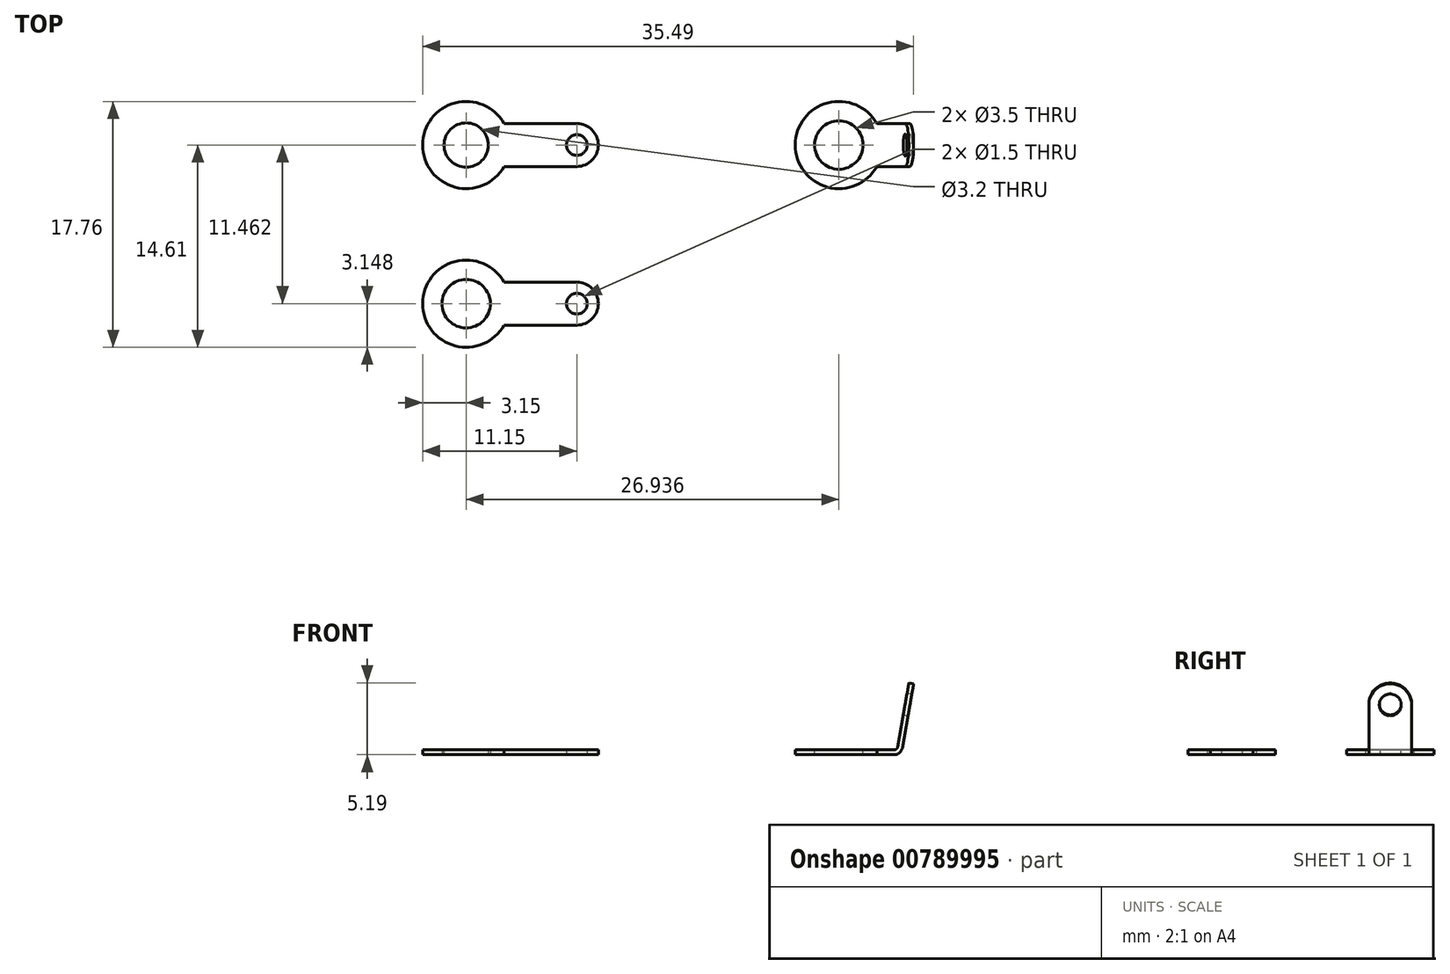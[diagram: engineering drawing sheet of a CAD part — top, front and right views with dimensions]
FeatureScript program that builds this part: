
annotation { "Feature Type Name" : "Feature", "Feature Type Description" : "" }
export const myFeature = defineFeature(function(context is Context, id is Id, definition is map)
    precondition{}
    {
        {
            var Q0;
            Q0=qCreatedBy(makeId("Top.planeOp"),FACE);
            var sketch = newSketch(context, id + "F0", { "sketchPlane" : qUnion([Q0])});
            skCircle(sketch, "E0", {"center": v(0, 0) * mm, "radius": 1.6 * mm});
            skCircle(sketch, "E1", {"center": v(0, 0) * mm, "radius": 3.15 * mm});
            skCircle(sketch, "E2", {"center": v(8, 0) * mm, "radius": 0.75 * mm});
            skCircle(sketch, "E3", {"center": v(8, 0) * mm, "radius": 1.55 * mm});
            skLineSegment(sketch, "E4", {"start": v(8, 1.55) * mm, "end": v(2.74, 1.55) * mm});
            skLineSegment(sketch, "E5", {"start": v(8, -1.55) * mm, "end": v(2.74, -1.55) * mm});
            skCircle(sketch, "E6", {"center": v(0, -11.46) * mm, "radius": 1.75 * mm});
            skCircle(sketch, "E7", {"center": v(0, -11.46) * mm, "radius": 3.15 * mm});
            skCircle(sketch, "E8", {"center": v(8, -11.46) * mm, "radius": 0.75 * mm});
            skCircle(sketch, "E9", {"center": v(8, -11.46) * mm, "radius": 1.55 * mm});
            skLineSegment(sketch, "E10", {"start": v(8, -9.91) * mm, "end": v(2.74, -9.91) * mm});
            skLineSegment(sketch, "E11", {"start": v(8, -13.01) * mm, "end": v(2.74, -13.01) * mm});
            skSolve(sketch);
        }
        {
            var Q0;
            Q0 = qSketchRegion(id + "F0", true);
            extrude(context, id + "F1", {"entities" : qUnion([Q0]), "depth" : .35 * mm, "offsetDistance" : 25 * mm});
        }
        {
            var Q0;
            Q0=qCreatedBy(makeId("Front.planeOp"),FACE);
            var sketch = newSketch(context, id + "F2", { "sketchPlane" : qUnion([Q0])});
            skLineSegment(sketch, "E12.bottom", {"start": v(23.79, 0.35) * mm, "end": v(30.94, 0.35) * mm});
            skLineSegment(sketch, "E12.top", {"start": v(23.79, 0) * mm, "end": v(30.94, 0) * mm});
            skLineSegment(sketch, "E12.left", {"start": v(23.79, 0.35) * mm, "end": v(23.79, 0) * mm});
            skLineSegment(sketch, "E12.right", {"start": v(30.94, 0.35) * mm, "end": v(30.94, 0) * mm});
            skLineSegment(sketch, "E13.bottom", {"start": v(31.18, 0.56) * mm, "end": v(31.53, 0.5) * mm});
            skLineSegment(sketch, "E13.top", {"start": v(32, 5.19) * mm, "end": v(32.34, 5.12) * mm});
            skLineSegment(sketch, "E13.left", {"start": v(31.18, 0.56) * mm, "end": v(32, 5.19) * mm});
            skLineSegment(sketch, "E13.right", {"start": v(31.53, 0.5) * mm, "end": v(32.34, 5.12) * mm});
            skLineSegment(sketch, "E14.bottom", {"start": v(25.19, 0.35) * mm, "end": v(28.69, 0.35) * mm});
            skLineSegment(sketch, "E14.top", {"start": v(25.19, 0) * mm, "end": v(28.69, 0) * mm});
            skLineSegment(sketch, "E14.left", {"start": v(25.19, 0.35) * mm, "end": v(25.19, 0) * mm});
            skLineSegment(sketch, "E14.right", {"start": v(28.69, 0.35) * mm, "end": v(28.69, 0) * mm});
            skLineSegment(sketch, "E15.bottom", {"start": v(31.87, 4.44) * mm, "end": v(32.21, 4.38) * mm});
            skLineSegment(sketch, "E15.top", {"start": v(31.6, 2.88) * mm, "end": v(31.94, 2.82) * mm});
            skLineSegment(sketch, "E15.left", {"start": v(31.87, 4.44) * mm, "end": v(31.6, 2.88) * mm});
            skLineSegment(sketch, "E15.right", {"start": v(32.21, 4.38) * mm, "end": v(31.94, 2.82) * mm});
            skCircle(sketch, "E16", {"center": v(30.94, 0.6) * mm, "radius": 0.25 * mm});
            skCircle(sketch, "E17", {"center": v(30.94, 0.6) * mm, "radius": 0.6 * mm});
            skLineSegment(sketch, "E18", {"start": v(26.94, 0.35) * mm, "end": v(26.94, 0) * mm});
            skLineSegment(sketch, "E19", {"start": v(31.73, 3.66) * mm, "end": v(32.07, 3.6) * mm});
            skLineSegment(sketch, "E20", {"start": v(26.94, 0.35) * mm, "end": v(26.94, 1.93) * mm, "construction": true});
            skLineSegment(sketch, "E21", {"start": v(31.9, 3.63) * mm, "end": v(31.73, 3.66) * mm, "construction": true});
            skPoint(sketch, "E21.endSnap0", {"position": v(31.9, 3.63) * mm});
            skSolve(sketch);
        }
        {
            var Q0;
            {var subQ0=sQuery(id+"F2.wireOp",EDGE,"E12.left");Q0=makeQuery(id+"F2.imprint","IMPRINT",FACE,{"disambiguationData":[TD([[makeQuery(id+"F2.imprint","IMPRINT",EDGE,{"derivedFrom":subQ0}),1.0]])]});}
            var Q1;
            Q1=sQuery(id+"F2.wireOp",EDGE,"E18");
            revolve(context, id + "F3", {"surfaceOperationType" : NewSurfaceOperationType.NEW, "entities" : qUnion([Q0]), "axis" : qUnion([Q1]), "revolveType" : RevolveType.FULL});
        }
        {
            var Q0;
            {var subQ0=sQuery(id+"F2.wireOp",EDGE,"E13.top");Q0=makeQuery(id+"F2.imprint","IMPRINT",FACE,{"disambiguationData":[TD([[makeQuery(id+"F2.imprint","IMPRINT",EDGE,{"derivedFrom":subQ0}),-1.0]])]});}
            var Q1;
            {var subQ0=sQuery(id+"F2.wireOp",EDGE,"E15.bottom");Q1=makeQuery(id+"F2.imprint","IMPRINT",FACE,{"disambiguationData":[TD([[makeQuery(id+"F2.imprint","IMPRINT",EDGE,{"derivedFrom":subQ0}),-1.0]])]});}
            var Q2;
            Q2=sQuery(id+"F2.wireOp",EDGE,"E19");
            revolve(context, id + "F4", {"surfaceOperationType" : NewSurfaceOperationType.NEW, "entities" : qUnion([Q0, Q1]), "axis" : qUnion([Q2]), "revolveType" : RevolveType.FULL});
        }
        {
            var Q0;
            {var subQ0=sQuery(id+"F2.wireOp",EDGE,"E15.top");Q0=makeQuery(id+"F2.imprint","IMPRINT",FACE,{"disambiguationData":[TD([[makeQuery(id+"F2.imprint","IMPRINT",EDGE,{"derivedFrom":subQ0}),-1.0]])]});}
            var Q1;
            {var subQ0=sQuery(id+"F2.wireOp",EDGE,"E12.right");Q1=makeQuery(id+"F2.imprint","IMPRINT",FACE,{"disambiguationData":[TD([[makeQuery(id+"F2.imprint","IMPRINT",EDGE,{"derivedFrom":subQ0}),1.0]])]});}
            var Q2;
            {var subQ0=sQuery(id+"F2.wireOp",EDGE,"E13.bottom");Q2=makeQuery(id+"F2.imprint","IMPRINT",FACE,{"disambiguationData":[TD([[makeQuery(id+"F2.imprint","IMPRINT",EDGE,{"derivedFrom":subQ0}),1.0]])]});}
            var Q3;
            {var subQ0=sQuery(id+"F2.wireOp",EDGE,"E12.right");Q3=makeQuery(id+"F2.imprint","IMPRINT",FACE,{"disambiguationData":[TD([[makeQuery(id+"F2.imprint","IMPRINT",EDGE,{"derivedFrom":subQ0}),-1.0]])]});}
            var Q4;
            {var subQ0=sQuery(id+"F2.wireOp",EDGE,"E14.right");Q4=makeQuery(id+"F2.imprint","IMPRINT",FACE,{"disambiguationData":[TD([[makeQuery(id+"F2.imprint","IMPRINT",EDGE,{"derivedFrom":subQ0}),1.0]])]});}
            var Q5;
            {var subQ0=sQuery(id+"F2.wireOp",EDGE,"E15.top");Q5=makeQuery(id+"F2.imprint","IMPRINT",FACE,{"disambiguationData":[TD([[makeQuery(id+"F2.imprint","IMPRINT",EDGE,{"derivedFrom":subQ0}),1.0]])]});}
            extrude(context, id + "F5", {"entities" : qUnion([Q0, Q1, Q2, Q3, Q4, Q5]), "operationType" : NewBodyOperationType.ADD, "endBound" : BoundingType.SYMMETRIC, "depth" : 3.1 * mm, "offsetDistance" : 25 * mm});
        }
        {
            var Q0;
            {var subQ0=sQuery(id+"F2.wireOp",EDGE,"E15.bottom");Q0=makeQuery(id+"F2.imprint","IMPRINT",FACE,{"disambiguationData":[TD([[makeQuery(id+"F2.imprint","IMPRINT",EDGE,{"derivedFrom":subQ0}),-1.0]])]});}
            var Q1;
            Q1=sQuery(id+"F2.wireOp",EDGE,"E19");
            revolve(context, id + "F6", {"operationType" : NewBodyOperationType.REMOVE, "surfaceOperationType" : NewSurfaceOperationType.NEW, "entities" : qUnion([Q0]), "axis" : qUnion([Q1]), "revolveType" : RevolveType.FULL, "oppositeDirection" : true});
        }
    });
